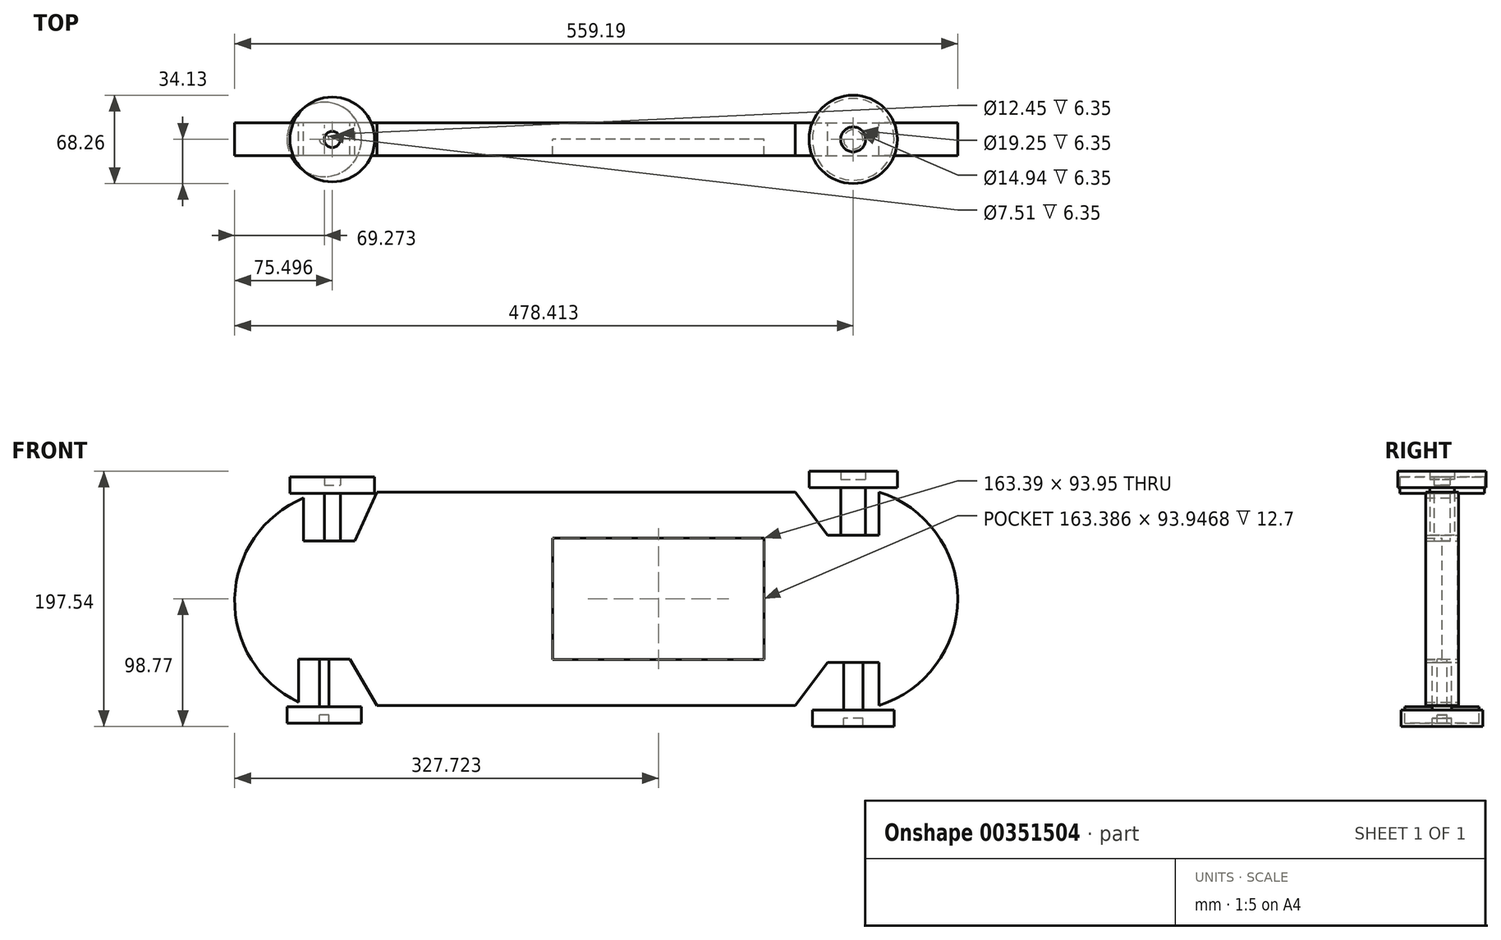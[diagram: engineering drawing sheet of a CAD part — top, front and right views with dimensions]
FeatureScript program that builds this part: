
annotation { "Feature Type Name" : "Feature", "Feature Type Description" : "" }
export const myFeature = defineFeature(function(context is Context, id is Id, definition is map)
    precondition{}
    {
        {
            var Q0;
            Q0=qCreatedBy(makeId("Front.planeOp"),FACE);
            var sketch = newSketch(context, id + "F0", { "sketchPlane" : qUnion([Q0])});
            skLineSegment(sketch, "E0.bottom", {"start": v(161.72, 82.55) * mm, "end": v(-161.72, 82.55) * mm});
            skLineSegment(sketch, "E0.top", {"start": v(161.72, -82.55) * mm, "end": v(-161.72, -82.55) * mm});
            skPoint(sketch, "E0.middle", {"position": v(0, 0) * mm});
            skLineSegment(sketch, "E1", {"start": v(-161.72, 82.55) * mm, "end": v(-178.91, 44.63) * mm});
            skLineSegment(sketch, "E2", {"start": v(161.72, 82.55) * mm, "end": v(186.7, 49.24) * mm});
            skLineSegment(sketch, "E3", {"start": v(-161.72, -82.55) * mm, "end": v(-182.81, -46.65) * mm});
            skLineSegment(sketch, "E4", {"start": v(161.72, -82.55) * mm, "end": v(186.7, -49.24) * mm});
            skLineSegment(sketch, "E5", {"start": v(-182.81, -46.65) * mm, "end": v(-222.44, -46.65) * mm});
            skLineSegment(sketch, "E6", {"start": v(-178.91, 44.63) * mm, "end": v(-218.54, 44.63) * mm});
            skLineSegment(sketch, "E7", {"start": v(-218.54, 44.63) * mm, "end": v(-218.54, 77.94) * mm});
            skLineSegment(sketch, "E8", {"start": v(-222.44, -46.65) * mm, "end": v(-222.44, -79.96) * mm});
            skLineSegment(sketch, "E9", {"start": v(186.7, 49.24) * mm, "end": v(226.33, 49.24) * mm});
            skLineSegment(sketch, "E10", {"start": v(186.7, -49.24) * mm, "end": v(226.33, -49.24) * mm});
            skLineSegment(sketch, "E11", {"start": v(226.33, 49.24) * mm, "end": v(226.33, 82.55) * mm});
            skLineSegment(sketch, "E12", {"start": v(226.33, -49.24) * mm, "end": v(226.33, -82.55) * mm});
            skArc(sketch, "E13", {"start": v(-218.54, 77.94) * mm, "mid": v(-271.88, 0.26) * mm, "end": v(-222.44, -79.96) * mm});
            skArc(sketch, "E14", {"start": v(226.33, -82.55) * mm, "mid": v(287.3, 0) * mm, "end": v(226.33, 82.55) * mm});
            skLineSegment(sketch, "E15.bottom", {"start": v(137.52, -46.97) * mm, "end": v(-25.87, -46.97) * mm});
            skLineSegment(sketch, "E15.top", {"start": v(137.52, 46.97) * mm, "end": v(-25.87, 46.97) * mm});
            skLineSegment(sketch, "E15.left", {"start": v(137.52, -46.97) * mm, "end": v(137.52, 46.97) * mm});
            skLineSegment(sketch, "E15.right", {"start": v(-25.87, -46.97) * mm, "end": v(-25.87, 46.97) * mm});
            skPoint(sketch, "E15.middle", {"position": v(55.82, 0) * mm});
            skLineSegment(sketch, "E16", {"start": v(-25.87, 19.92) * mm, "end": v(137.52, 19.92) * mm});
            skLineSegment(sketch, "E17", {"start": v(-25.87, -14.86) * mm, "end": v(137.52, -14.86) * mm});
            skLineSegment(sketch, "E18", {"start": v(-206.38, -46.65) * mm, "end": v(-206.38, -89.83) * mm});
            skLineSegment(sketch, "E19", {"start": v(-202.63, -46.65) * mm, "end": v(-202.63, -89.83) * mm});
            skLineSegment(sketch, "E20", {"start": v(-206.38, -89.83) * mm, "end": v(-202.63, -89.83) * mm});
            skLineSegment(sketch, "E21", {"start": v(-202.63, 44.63) * mm, "end": v(-202.63, 87.8) * mm});
            skLineSegment(sketch, "E22", {"start": v(-196.4, 44.63) * mm, "end": v(-196.4, 87.8) * mm});
            skLineSegment(sketch, "E23", {"start": v(-196.4, 87.8) * mm, "end": v(-202.63, 87.8) * mm});
            skLineSegment(sketch, "E24", {"start": v(206.51, -49.24) * mm, "end": v(206.51, -92.42) * mm});
            skLineSegment(sketch, "E25", {"start": v(199.05, -49.24) * mm, "end": v(199.05, -92.42) * mm});
            skLineSegment(sketch, "E26", {"start": v(199.05, -92.42) * mm, "end": v(206.51, -92.42) * mm});
            skLineSegment(sketch, "E27", {"start": v(206.51, 49.24) * mm, "end": v(206.51, 92.42) * mm});
            skLineSegment(sketch, "E28", {"start": v(206.51, 92.42) * mm, "end": v(196.89, 92.42) * mm});
            skLineSegment(sketch, "E29", {"start": v(196.89, 92.42) * mm, "end": v(196.89, 49.24) * mm});
            skSolve(sketch);
        }
        {
            var Q0;
            Q0=makeQuery(id+"F0.imprint","IMPRINT",FACE,{"disambiguationData":[TD([[makeQuery(id+"F0.imprint","IMPRINT",EDGE,{"derivedFrom":sQuery(id+"F0.wireOp",EDGE,"E0.bottom")}),1.0]])]});
            extrude(context, id + "F1", {"entities" : qUnion([Q0]), "endBound" : BoundingType.SYMMETRIC, "depth" : 25.4 * mm});
        }
        {
            var Q0;
            {var subQ0=sQuery(id+"F0.wireOp",EDGE,"E15.top");Q0=makeQuery(id+"F0.imprint","IMPRINT",FACE,{"disambiguationData":[TD([[makeQuery(id+"F0.imprint","IMPRINT",EDGE,{"derivedFrom":subQ0}),1.0]])]});}
            var Q1;
            {var subQ0=sQuery(id+"F0.wireOp",EDGE,"E16");Q1=makeQuery(id+"F0.imprint","IMPRINT",FACE,{"disambiguationData":[TD([[makeQuery(id+"F0.imprint","IMPRINT",EDGE,{"derivedFrom":subQ0}),-1.0]])]});}
            var Q2;
            {var subQ0=sQuery(id+"F0.wireOp",EDGE,"E15.bottom");Q2=makeQuery(id+"F0.imprint","IMPRINT",FACE,{"disambiguationData":[TD([[makeQuery(id+"F0.imprint","IMPRINT",EDGE,{"derivedFrom":subQ0}),-1.0]])]});}
            extrude(context, id + "F2", {"entities" : qUnion([Q0, Q1, Q2]), "operationType" : NewBodyOperationType.ADD, "oppositeDirection" : true, "depth" : 12.2 * mm});
        }
        {
            var Q0;
            {var subQ0=sQuery(id+"F0.wireOp",EDGE,"E21");Q0=makeQuery(id+"F0.imprint","IMPRINT",FACE,{"disambiguationData":[TD([[makeQuery(id+"F0.imprint","IMPRINT",EDGE,{"derivedFrom":subQ0}),-1.0]])]});}
            var Q1;
            Q1=sQuery(id+"F0.wireOp",EDGE,"E22");
            revolve(context, id + "F3", {"operationType" : NewBodyOperationType.ADD, "entities" : qUnion([Q0]), "axis" : qUnion([Q1]), "revolveType" : RevolveType.FULL});
        }
        {
            var Q0;
            {var subQ0=sQuery(id+"F0.wireOp",EDGE,"E18");Q0=makeQuery(id+"F0.imprint","IMPRINT",FACE,{"disambiguationData":[TD([[makeQuery(id+"F0.imprint","IMPRINT",EDGE,{"derivedFrom":subQ0}),1.0]])]});}
            var Q1;
            Q1=sQuery(id+"F0.wireOp",EDGE,"E19");
            revolve(context, id + "F4", {"operationType" : NewBodyOperationType.ADD, "entities" : qUnion([Q0]), "axis" : qUnion([Q1]), "revolveType" : RevolveType.FULL});
        }
        {
            var Q0;
            {var subQ0=sQuery(id+"F0.wireOp",EDGE,"E27");Q0=makeQuery(id+"F0.imprint","IMPRINT",FACE,{"disambiguationData":[TD([[makeQuery(id+"F0.imprint","IMPRINT",EDGE,{"derivedFrom":subQ0}),1.0]])]});}
            var Q1;
            Q1=sQuery(id+"F0.wireOp",EDGE,"E27");
            revolve(context, id + "F5", {"operationType" : NewBodyOperationType.ADD, "entities" : qUnion([Q0]), "axis" : qUnion([Q1]), "revolveType" : RevolveType.FULL});
        }
        {
            var Q0;
            {var subQ0=sQuery(id+"F0.wireOp",EDGE,"E24");Q0=makeQuery(id+"F0.imprint","IMPRINT",FACE,{"disambiguationData":[TD([[makeQuery(id+"F0.imprint","IMPRINT",EDGE,{"derivedFrom":subQ0}),-1.0]])]});}
            var Q1;
            Q1=sQuery(id+"F0.wireOp",EDGE,"E24");
            revolve(context, id + "F6", {"operationType" : NewBodyOperationType.ADD, "entities" : qUnion([Q0]), "axis" : qUnion([Q1]), "revolveType" : RevolveType.FULL});
        }
        {
            var Q0;
            Q0=makeQuery(id+"F3.opRevolve","SWEPT_FACE",FACE,{"disambiguationData":[OSD([sQuery(id+"F0.wireOp",EDGE,"E23")])]});
            var sketch = newSketch(context, id + "F7", { "sketchPlane" : qUnion([Q0])});
            skCircle(sketch, "E30", {"center": v(-196.4, 0) * mm, "radius": 32.78 * mm});
            skSolve(sketch);
        }
        {
            var Q0;
            Q0=makeQuery(id+"F7.imprint","IMPRINT",FACE,{"disambiguationData":[TD([[makeQuery(id+"F7.imprint","IMPRINT",EDGE,{"derivedFrom":sQuery(id+"F7.wireOp",EDGE,"E30")}),1.0]])]});
            extrude(context, id + "F8", {"entities" : qUnion([Q0]), "operationType" : NewBodyOperationType.ADD, "endBound" : BoundingType.SYMMETRIC, "depth" : 12.7 * mm});
        }
        {
            var Q0;
            Q0=makeQuery(id+"F5.opRevolve","SWEPT_FACE",FACE,{"disambiguationData":[OSD([sQuery(id+"F0.wireOp",EDGE,"E28")])]});
            var sketch = newSketch(context, id + "F9", { "sketchPlane" : qUnion([Q0])});
            skCircle(sketch, "E31", {"center": v(206.51, 0) * mm, "radius": 34.13 * mm});
            skSolve(sketch);
        }
        {
            var Q0;
            Q0=makeQuery(id+"F9.imprint","IMPRINT",FACE,{"disambiguationData":[TD([[makeQuery(id+"F9.imprint","IMPRINT",EDGE,{"derivedFrom":sQuery(id+"F9.wireOp",EDGE,"E31")}),1.0]])]});
            extrude(context, id + "F10", {"entities" : qUnion([Q0]), "operationType" : NewBodyOperationType.ADD, "endBound" : BoundingType.SYMMETRIC, "depth" : 12.7 * mm});
        }
        {
            var Q0;
            Q0=makeQuery(id+"F6.opRevolve","SWEPT_FACE",FACE,{"disambiguationData":[OSD([sQuery(id+"F0.wireOp",EDGE,"E26")])]});
            var sketch = newSketch(context, id + "F11", { "sketchPlane" : qUnion([Q0])});
            skCircle(sketch, "E32", {"center": v(206.51, 0) * mm, "radius": 31.6 * mm});
            skSolve(sketch);
        }
        {
            var Q0;
            Q0=makeQuery(id+"F11.imprint","IMPRINT",FACE,{"disambiguationData":[TD([[makeQuery(id+"F11.imprint","IMPRINT",EDGE,{"derivedFrom":sQuery(id+"F11.wireOp",EDGE,"E32")}),1.0]])]});
            extrude(context, id + "F12", {"entities" : qUnion([Q0]), "operationType" : NewBodyOperationType.ADD, "endBound" : BoundingType.SYMMETRIC, "depth" : 12.7 * mm});
        }
        {
            var Q0;
            Q0=makeQuery(id+"F4.opRevolve","SWEPT_FACE",FACE,{"disambiguationData":[OSD([sQuery(id+"F0.wireOp",EDGE,"E20")])]});
            var sketch = newSketch(context, id + "F13", { "sketchPlane" : qUnion([Q0])});
            skCircle(sketch, "E33", {"center": v(-202.63, 0) * mm, "radius": 28.78 * mm});
            skSolve(sketch);
        }
        {
            var Q0;
            Q0=makeQuery(id+"F13.imprint","IMPRINT",FACE,{"disambiguationData":[TD([[makeQuery(id+"F13.imprint","IMPRINT",EDGE,{"derivedFrom":sQuery(id+"F13.wireOp",EDGE,"E33")}),1.0]])]});
            extrude(context, id + "F14", {"entities" : qUnion([Q0]), "operationType" : NewBodyOperationType.ADD, "endBound" : BoundingType.SYMMETRIC, "depth" : 12.7 * mm});
        }
    });
